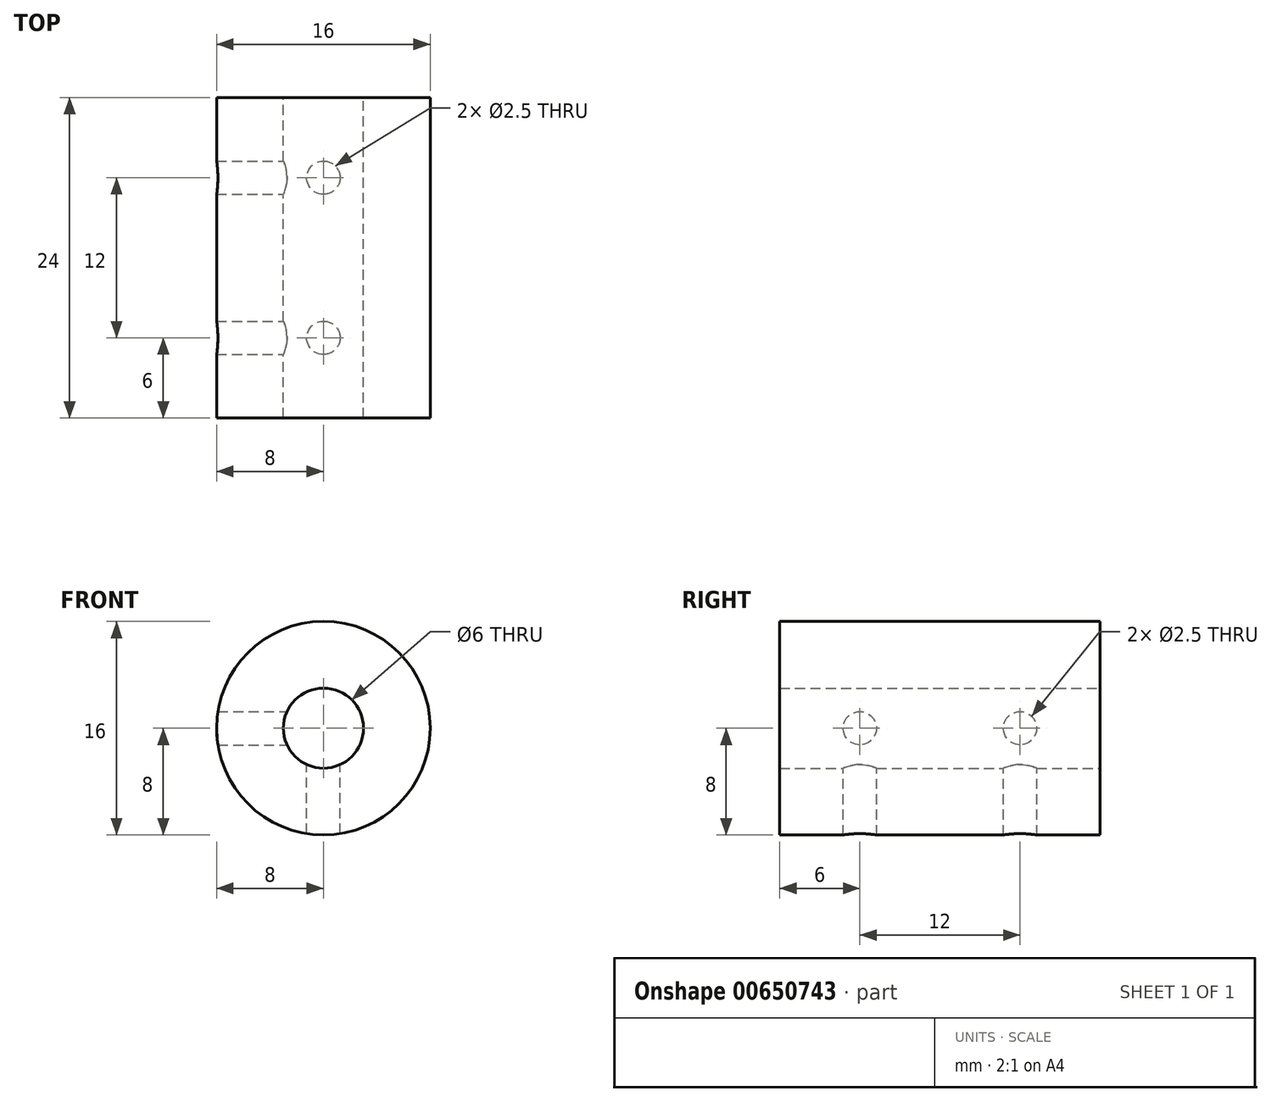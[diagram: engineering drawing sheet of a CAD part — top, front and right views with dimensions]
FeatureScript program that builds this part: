
annotation { "Feature Type Name" : "Feature", "Feature Type Description" : "" }
export const myFeature = defineFeature(function(context is Context, id is Id, definition is map)
    precondition{}
    {
        {
            var Q0;
            Q0=qCreatedBy(makeId("Front.planeOp"),FACE);
            var sketch = newSketch(context, id + "F0", { "sketchPlane" : qUnion([Q0])});
            skCircle(sketch, "E0", {"center": v(0, 0) * mm, "radius": 8 * mm});
            skSolve(sketch);
        }
        {
            var Q0;
            Q0 = qSketchRegion(id + "F0", true);
            extrude(context, id + "F1", {"entities" : qUnion([Q0]), "depth" : 24 * mm, "offsetDistance" : 25 * mm});
        }
        {
            var Q0;
            Q0=qCreatedBy(makeId("Front.planeOp"),FACE);
            var sketch = newSketch(context, id + "F2", { "sketchPlane" : qUnion([Q0])});
            skCircle(sketch, "E1", {"center": v(0, 0) * mm, "radius": 3 * mm});
            skSolve(sketch);
        }
        {
            var Q0;
            Q0 = qSketchRegion(id + "F2", true);
            extrude(context, id + "F3", {"entities" : qUnion([Q0]), "operationType" : NewBodyOperationType.REMOVE, "endBound" : BoundingType.THROUGH_ALL, "depth" : 25 * mm, "offsetDistance" : 25 * mm});
        }
        {
            var Q0;
            Q0=qCreatedBy(makeId("Right.planeOp"),FACE);
            var sketch = newSketch(context, id + "F4", { "sketchPlane" : qUnion([Q0])});
            skLineSegment(sketch, "E2", {"start": v(0, 0) * mm, "end": v(-28.12, 0) * mm, "construction": true});
            skPoint(sketch, "E3", {"position": v(-6, 0) * mm});
            skPoint(sketch, "E4", {"position": v(-18, 0) * mm});
            skSolve(sketch);
        }
        {
            var Q0;
            Q0=sQuery(id+"F4.wireOp",VERTEX,"E4");
            var Q1;
            Q1=sQuery(id+"F4.wireOp",VERTEX,"E3");
            var Q2;
            Q2=makeQuery(id+"F1.opExtrude","SWEPT_BODY",BODY,{"disambiguationData":[OSD([sQuery(id+"F0.wireOp",EDGE,"E0")])]});
            hole(context, id + "F5", {"style" : HoleStyle.SIMPLE, "endStyle" : HoleEndStyle.THROUGH, "standardTappedOrClearance" : lookupTablePath({ "standard" : "ISO", "engagement" : "75%", "pitch" : "0.5 mm", "size" : "M3", "type" : "Tapped" }), "standardBlindInLast" : lookupTablePath({ "standard" : "ISO", "engagement" : "75%", "pitch" : "0.5 mm", "size" : "M3", "type" : "Tapped" }), "holeDiameter" : 2.5 * mm, "majorDiameter" : 3 * mm, "showTappedDepth" : true, "isTappedThrough" : true, "tappedDepth" : 5.5 * mm, "tapClearance" : 3, "locations" : qUnion([Q0, Q1]), "scope" : qUnion([Q2])});
        }
        {
            var Q0;
            Q0=qCreatedBy(makeId("Top.planeOp"),FACE);
            var sketch = newSketch(context, id + "F6", { "sketchPlane" : qUnion([Q0])});
            skLineSegment(sketch, "E5", {"start": v(0, 0) * mm, "end": v(0, -36) * mm, "construction": true});
            skPoint(sketch, "E6", {"position": v(0, -6) * mm});
            skPoint(sketch, "E7", {"position": v(0, -18) * mm});
            skSolve(sketch);
        }
        {
            var Q0;
            Q0=sQuery(id+"F6.wireOp",VERTEX,"E7");
            var Q1;
            Q1=sQuery(id+"F6.wireOp",VERTEX,"E6");
            var Q2;
            Q2=makeQuery(id+"F1.opExtrude","SWEPT_BODY",BODY,{"disambiguationData":[OSD([sQuery(id+"F0.wireOp",EDGE,"E0")])]});
            hole(context, id + "F7", {"style" : HoleStyle.SIMPLE, "endStyle" : HoleEndStyle.THROUGH, "standardTappedOrClearance" : lookupTablePath({ "standard" : "ISO", "engagement" : "75%", "pitch" : "0.5 mm", "size" : "M3", "type" : "Tapped" }), "standardBlindInLast" : lookupTablePath({ "standard" : "ISO", "engagement" : "75%", "pitch" : "0.5 mm", "size" : "M3", "type" : "Tapped" }), "holeDiameter" : 2.5 * mm, "majorDiameter" : 3 * mm, "showTappedDepth" : true, "isTappedThrough" : true, "tappedDepth" : 5.5 * mm, "tapClearance" : 3, "locations" : qUnion([Q0, Q1]), "scope" : qUnion([Q2])});
        }
    });
